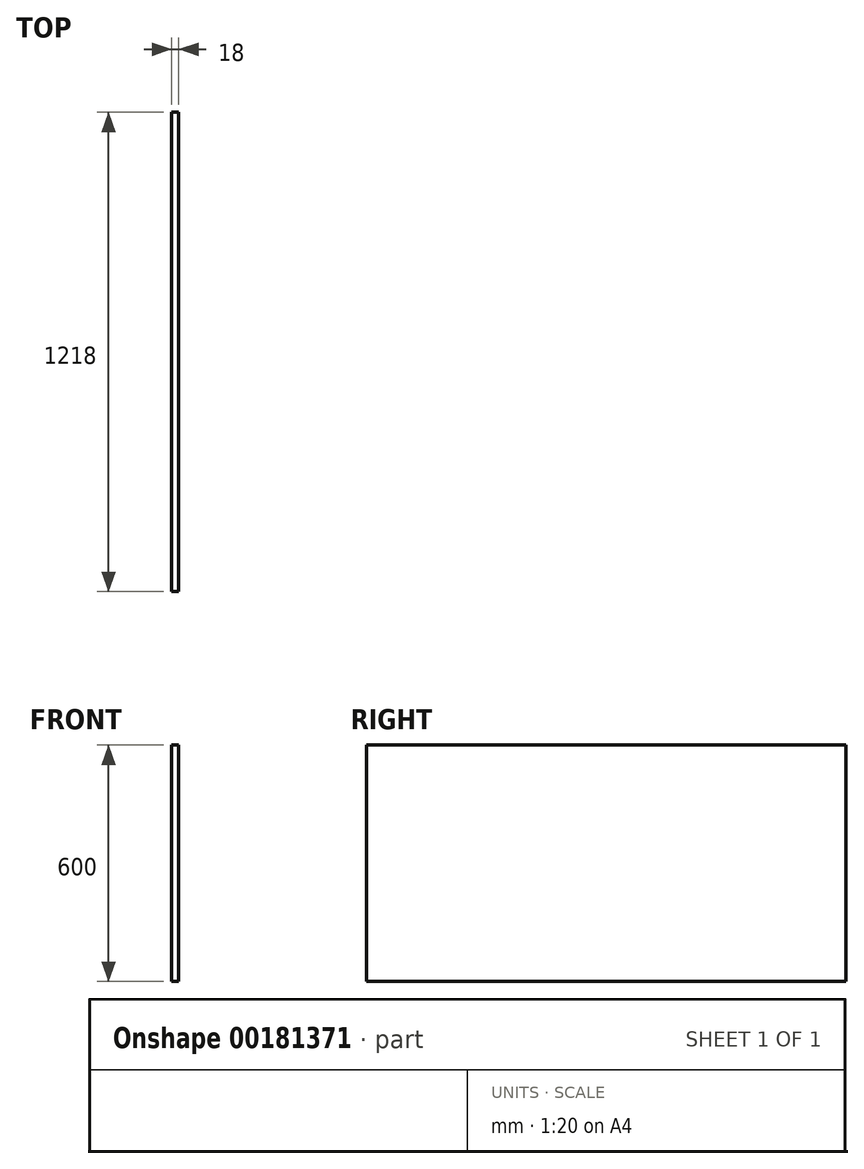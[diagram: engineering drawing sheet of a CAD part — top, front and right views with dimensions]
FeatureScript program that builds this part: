
annotation { "Feature Type Name" : "Feature", "Feature Type Description" : "" }
export const myFeature = defineFeature(function(context is Context, id is Id, definition is map)
    precondition{}
    {
        {
            var Q0;
            Q0=qCreatedBy(makeId("Right.planeOp"),FACE);
            var sketch = newSketch(context, id + "F0", { "sketchPlane" : qUnion([Q0])});
            skLineSegment(sketch, "E0.bottom", {"start": v(-609, 300) * mm, "end": v(609, 300) * mm});
            skLineSegment(sketch, "E0.top", {"start": v(-609, -300) * mm, "end": v(609, -300) * mm});
            skLineSegment(sketch, "E0.left", {"start": v(-609, 300) * mm, "end": v(-609, -300) * mm});
            skLineSegment(sketch, "E0.right", {"start": v(609, 300) * mm, "end": v(609, -300) * mm});
            skPoint(sketch, "E0.middle", {"position": v(0, 0) * mm});
            skSolve(sketch);
        }
        {
            var Q0;
            Q0 = qSketchRegion(id + "F0", true);
            extrude(context, id + "F1", {"entities" : qUnion([Q0]), "depth" : 18 * mm});
        }
    });
